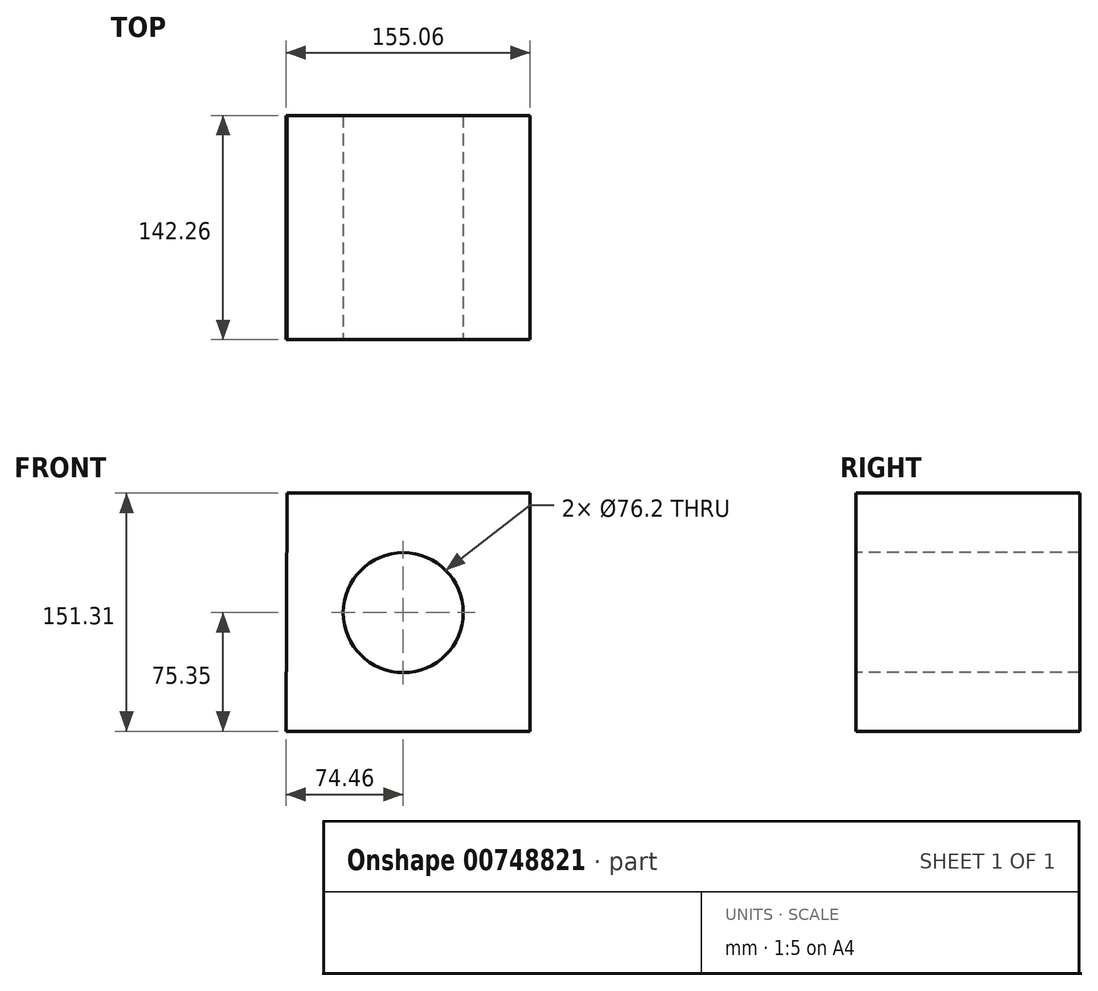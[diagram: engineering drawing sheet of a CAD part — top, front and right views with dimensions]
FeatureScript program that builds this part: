
annotation { "Feature Type Name" : "Feature", "Feature Type Description" : "" }
export const myFeature = defineFeature(function(context is Context, id is Id, definition is map)
    precondition{}
    {
        {
            var Q0;
            Q0=qCreatedBy(makeId("Front.planeOp"),FACE);
            var sketch = newSketch(context, id + "F0", { "sketchPlane" : qUnion([Q0])});
            skLineSegment(sketch, "E0", {"start": v(-73.98, 76.46) * mm, "end": v(-73.98, -77.82) * mm});
            skLineSegment(sketch, "E1", {"start": v(-73.98, -77.82) * mm, "end": v(80.27, -77.82) * mm});
            skLineSegment(sketch, "E2", {"start": v(80.27, -77.82) * mm, "end": v(80.27, 78.13) * mm});
            skLineSegment(sketch, "E3", {"start": v(80.27, 78.13) * mm, "end": v(-73.98, 76.46) * mm});
            skSolve(sketch);
        }
        {
            var Q0;
            Q0=makeQuery(id+"F0.imprint","IMPRINT",FACE,{"disambiguationData":[TD([[makeQuery(id+"F0.imprint","IMPRINT",EDGE,{"derivedFrom":sQuery(id+"F0.wireOp",EDGE,"E0")}),1.0]])]});
            var sketch = newSketch(context, id + "F1", { "sketchPlane" : qUnion([Q0])});
            skLineSegment(sketch, "E4", {"start": v(-73.8, 75.96) * mm, "end": v(80.6, 75.96) * mm});
            skLineSegment(sketch, "E5", {"start": v(80.6, 75.96) * mm, "end": v(80.6, -75.35) * mm});
            skLineSegment(sketch, "E6", {"start": v(80.6, -75.35) * mm, "end": v(-74.46, -75.35) * mm});
            skLineSegment(sketch, "E7", {"start": v(-74.46, -75.35) * mm, "end": v(-73.8, 75.96) * mm});
            skSolve(sketch);
        }
        {
            var Q0;
            Q0 = qSketchRegion(id + "F1", true);
            extrude(context, id + "F2", {"entities" : qUnion([Q0]), "depth" : 142.26 * mm, "offsetDistance" : 25.4 * mm});
        }
        {
            var Q0;
            Q0=makeQuery(id+"F2.opExtrude","CAP_FACE",FACE,{"disambiguationData":[OSD([sQuery(id+"F1.wireOp",EDGE,"E4"),sQuery(id+"F1.wireOp",EDGE,"E5"),sQuery(id+"F1.wireOp",EDGE,"E6"),sQuery(id+"F1.wireOp",EDGE,"E7")])],"isStart":false});
            var sketch = newSketch(context, id + "F3", { "sketchPlane" : qUnion([Q0])});
            skPoint(sketch, "E8", {"position": v(0, 0) * mm});
            skSolve(sketch);
        }
        {
            var Q0;
            Q0=sQuery(id+"F3.wireOp",VERTEX,"E8");
            var Q1;
            Q1=makeQuery(id+"F2.opExtrude","SWEPT_BODY",BODY,{"disambiguationData":[OSD([sQuery(id+"F1.wireOp",EDGE,"E4"),sQuery(id+"F1.wireOp",EDGE,"E5"),sQuery(id+"F1.wireOp",EDGE,"E6"),sQuery(id+"F1.wireOp",EDGE,"E7")])]});
            hole(context, id + "F4", {"style" : HoleStyle.SIMPLE, "endStyle" : HoleEndStyle.THROUGH, "standardTappedOrClearance" : lookupTablePath({ "fit" : "Normal", "standard" : "Custom", "size" : "1/4", "type" : "Clearance" }), "standardBlindInLast" : lookupTablePath({ "fit" : "Free", "standard" : "Custom", "size" : "1/4", "type" : "Clearance" }), "holeDiameter" : 76.2 * mm, "majorDiameter" : 6.35 * mm, "isTappedThrough" : true, "tappedDepth" : 12.7 * mm, "tapClearance" : 3, "locations" : qUnion([Q0]), "scope" : qUnion([Q1])});
        }
    });
